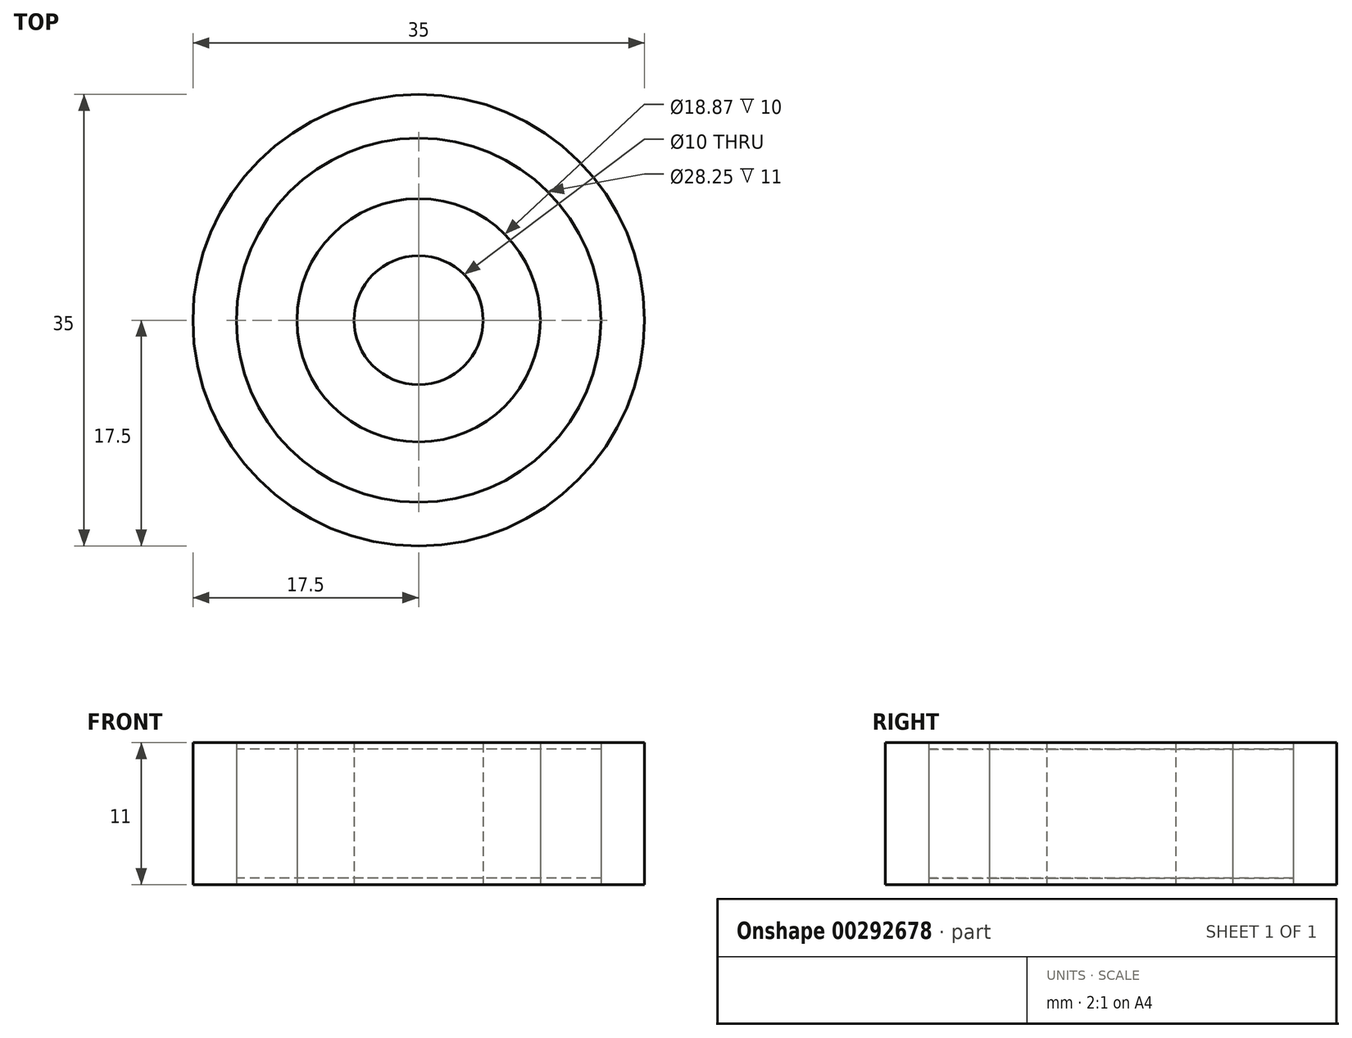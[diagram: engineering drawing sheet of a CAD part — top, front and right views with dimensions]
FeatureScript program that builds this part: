
annotation { "Feature Type Name" : "Feature", "Feature Type Description" : "" }
export const myFeature = defineFeature(function(context is Context, id is Id, definition is map)
    precondition{}
    {
        {
            var Q0;
            Q0=qCreatedBy(makeId("Top.planeOp"),FACE);
            var sketch = newSketch(context, id + "F0", { "sketchPlane" : qUnion([Q0])});
            skCircle(sketch, "E0", {"center": v(0, 0) * mm, "radius": 5 * mm});
            skCircle(sketch, "E1", {"center": v(0, 0) * mm, "radius": 17.5 * mm});
            skCircle(sketch, "E2", {"center": v(0, 0) * mm, "radius": 9.43 * mm});
            skCircle(sketch, "E3", {"center": v(0, 0) * mm, "radius": 14.12 * mm});
            skSolve(sketch);
        }
        {
            var Q0;
            Q0=makeQuery(id+"F0.imprint","IMPRINT",FACE,{"disambiguationData":[TD([[makeQuery(id+"F0.imprint","IMPRINT",EDGE,{"derivedFrom":sQuery(id+"F0.wireOp",EDGE,"E0")}),-1.0]])]});
            var Q1;
            Q1=makeQuery(id+"F0.imprint","IMPRINT",FACE,{"disambiguationData":[TD([[makeQuery(id+"F0.imprint","IMPRINT",EDGE,{"derivedFrom":sQuery(id+"F0.wireOp",EDGE,"E1")}),1.0]])]});
            extrude(context, id + "F1", {"entities" : qUnion([Q0, Q1]), "depth" : 11 * mm, "offsetDistance" : 25 * mm});
        }
        {
            var Q0;
            Q0=makeQuery(id+"F0.imprint","IMPRINT",FACE,{"disambiguationData":[TD([[makeQuery(id+"F0.imprint","IMPRINT",EDGE,{"derivedFrom":sQuery(id+"F0.wireOp",EDGE,"E2")}),-1.0]])]});
            var Q1;
            Q1=makeQuery(id+"F1.opExtrude","CAP_FACE",FACE,{"disambiguationData":[OSD([sQuery(id+"F0.wireOp",EDGE,"E0"),sQuery(id+"F0.wireOp",EDGE,"E2")])],"isStart":false});
            extrude(context, id + "F2", {"entities" : qUnion([Q0]), "endBound" : BoundingType.UP_TO_SURFACE, "depth" : 25 * mm, "endBoundEntityFace" : qUnion([Q1]), "hasOffset" : true, "offsetDistance" : 0.5 * mm, "hasSecondDirection" : true, "secondDirectionOppositeDirection" : false, "secondDirectionDepth" : 0.5 * mm});
        }
    });
